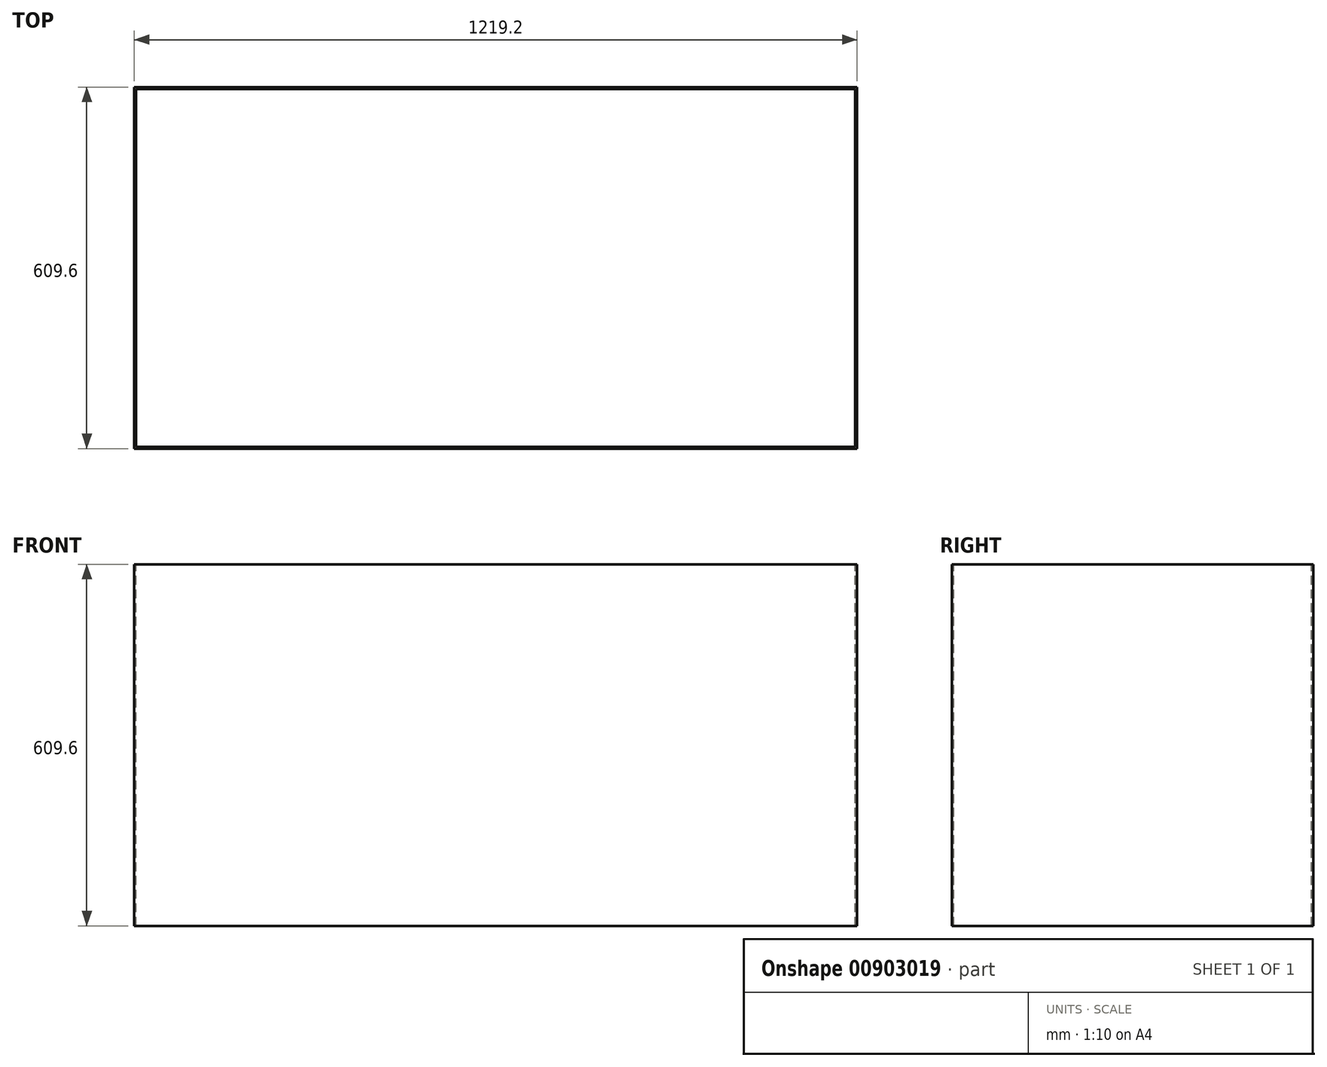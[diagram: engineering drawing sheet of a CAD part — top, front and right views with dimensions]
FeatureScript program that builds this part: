
annotation { "Feature Type Name" : "Feature", "Feature Type Description" : "" }
export const myFeature = defineFeature(function(context is Context, id is Id, definition is map)
    precondition{}
    {
        {
            var Q0;
            Q0=qCreatedBy(makeId("Top.planeOp"),FACE);
            var sketch = newSketch(context, id + "F0", { "sketchPlane" : qUnion([Q0])});
            skLineSegment(sketch, "E0.bottom", {"start": v(609.6, 304.8) * mm, "end": v(-609.6, 304.8) * mm});
            skLineSegment(sketch, "E0.top", {"start": v(609.6, -304.8) * mm, "end": v(-609.6, -304.8) * mm});
            skLineSegment(sketch, "E0.left", {"start": v(609.6, 304.8) * mm, "end": v(609.6, -304.8) * mm});
            skLineSegment(sketch, "E0.right", {"start": v(-609.6, 304.8) * mm, "end": v(-609.6, -304.8) * mm});
            skPoint(sketch, "E0.middle", {"position": v(0, 0) * mm});
            skSolve(sketch);
        }
        {
            var Q0;
            Q0=makeQuery(id+"F0.imprint","IMPRINT",FACE,{"disambiguationData":[TD([[makeQuery(id+"F0.imprint","IMPRINT",EDGE,{"derivedFrom":sQuery(id+"F0.wireOp",EDGE,"E0.bottom")}),1.0]])]});
            var sketch = newSketch(context, id + "F1", { "sketchPlane" : qUnion([Q0])});
            skLineSegment(sketch, "E1.bottom", {"start": v(606.42, 301.63) * mm, "end": v(-606.42, 301.63) * mm});
            skLineSegment(sketch, "E1.top", {"start": v(606.42, -301.63) * mm, "end": v(-606.42, -301.63) * mm});
            skLineSegment(sketch, "E1.left", {"start": v(606.43, 301.63) * mm, "end": v(606.43, -301.63) * mm});
            skLineSegment(sketch, "E1.right", {"start": v(-606.42, 301.63) * mm, "end": v(-606.42, -301.63) * mm});
            skPoint(sketch, "E1.middle", {"position": v(0, 0) * mm});
            skSolve(sketch);
        }
        {
            var Q0;
            Q0=sQuery(id+"F0.wireOp",EDGE,"E0.right");
            var Q1;
            Q1=sQuery(id+"F1.wireOp",EDGE,"E1.right");
            var Q2;
            Q2=sQuery(id+"F0.wireOp",EDGE,"E0.top");
            var Q3;
            Q3=sQuery(id+"F1.wireOp",EDGE,"E1.top");
            var Q4;
            Q4=sQuery(id+"F1.wireOp",EDGE,"E1.bottom");
            var Q5;
            Q5=sQuery(id+"F0.wireOp",EDGE,"E0.bottom");
            var Q6;
            Q6=sQuery(id+"F0.wireOp",EDGE,"E0.left");
            var Q7;
            Q7=sQuery(id+"F1.wireOp",EDGE,"E1.left");
            extrude(context, id + "F2", {"bodyType" : ToolBodyType.SURFACE, "surfaceEntities" : qUnion([Q0, Q1, Q2, Q3, Q4, Q5, Q6, Q7]), "depth" : 609.6 * mm, "offsetDistance" : 25.4 * mm});
        }
    });
